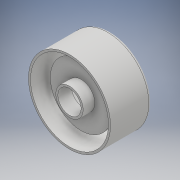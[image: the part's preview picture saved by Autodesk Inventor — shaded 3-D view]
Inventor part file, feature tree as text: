
AUTODESK INVENTOR PART (.ipt)
format: ipt  version: 2017 (Build 210142000, 142)  size: 158,720 bytes
history: native  units: mm
features: extrude x2, fillet x2, sketch x2, shell x1
ambient origin geometry x8: Origin, YZ Plane, XZ Plane, XY Plane, X Axis, Y Axis, Z Axis, Center Point
bodies: Solid1 (feature_tree)
feature tree (7):
  extrude  "Extrusion1"  Depth=17.0mm
  extrude  "Extrusion2"  Depth=1.5mm
  fillet  "Fillet1"  Radius=20.0mm
  fillet  "Fillet2"  Radius=2.0mm
  shell  "Shell2"  Thickness=0.5mm
  sketch  "Sketch1"  dims[d0=60.0mm d1=17.0mm]
  sketch  "Sketch2"  dims[d2=30.0mm d3=0.0mm d4=42.0mm d5=20.0mm d6=0.0mm d7=2.0mm d8=0.5mm d10=1.5mm]
